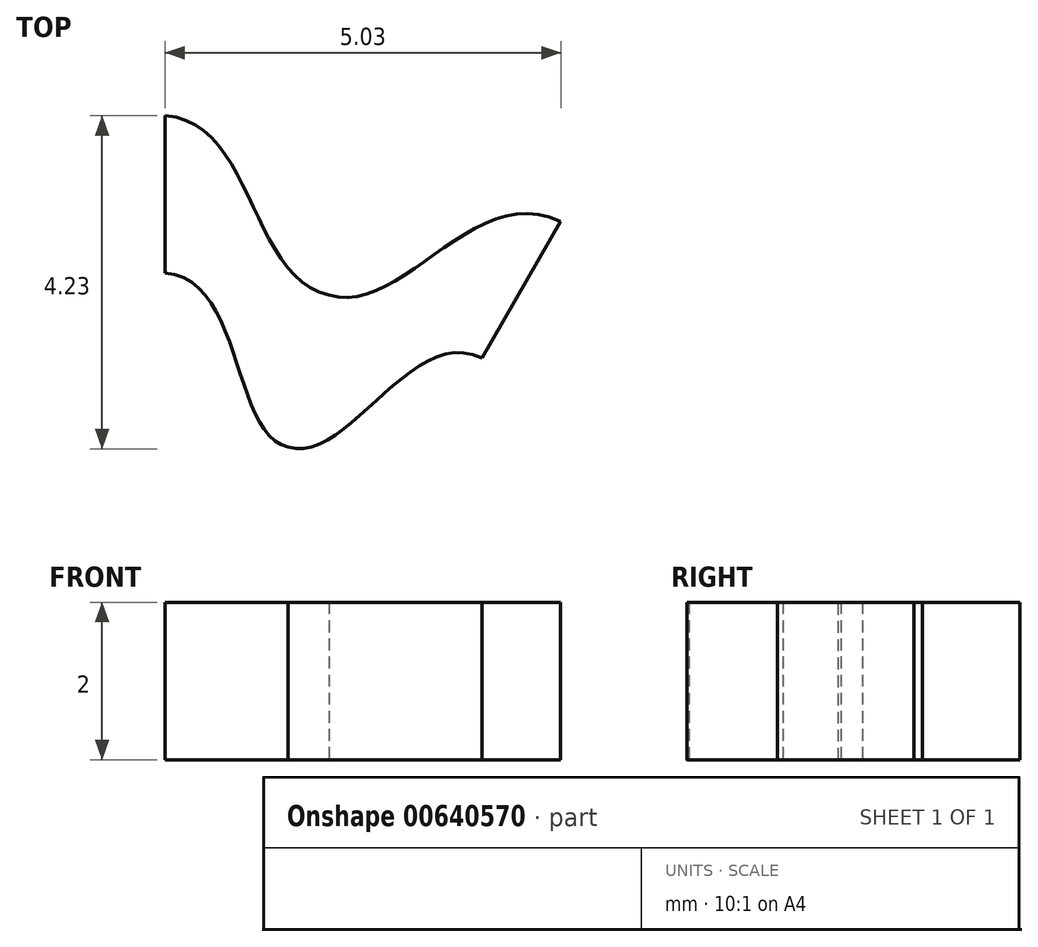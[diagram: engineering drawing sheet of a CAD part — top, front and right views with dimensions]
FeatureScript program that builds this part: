
annotation { "Feature Type Name" : "Feature", "Feature Type Description" : "" }
export const myFeature = defineFeature(function(context is Context, id is Id, definition is map)
    precondition{}
    {
        {
            var Q0;
            Q0=qCreatedBy(makeId("Top.planeOp"),FACE);
            var sketch = newSketch(context, id + "F0", { "sketchPlane" : qUnion([Q0])});
            skCircle(sketch, "E0", {"center": v(0, 0) * mm, "radius": 8.05 * mm, "construction": true});
            skLineSegment(sketch, "E1", {"start": v(0, 0) * mm, "end": v(3.4, 12.7) * mm, "construction": true});
            skLineSegment(sketch, "E2", {"start": v(0, 0) * mm, "end": v(6.53, 11.3) * mm, "construction": true});
            skLineSegment(sketch, "E3", {"start": v(0, 8.05) * mm, "end": v(0, 10.05) * mm});
            skLineSegment(sketch, "E4", {"start": v(2.08, 7.78) * mm, "end": v(1.57, 5.84) * mm});
            skLineSegment(sketch, "E5", {"start": v(4.02, 6.97) * mm, "end": v(5.02, 8.7) * mm});
            skFitSpline(sketch, "E6", {"points": [v(0, 10.05) * mm, v(2.08, 7.78) * mm], "startDerivative": vector(3.37, -0.19) * mm, "endDerivative": vector(3, -0.6) * mm});
            skFitSpline(sketch, "E7", {"points": [v(2.08, 7.78) * mm, v(5.03, 8.7) * mm], "startDerivative": vector(2.71, -0.9) * mm, "endDerivative": vector(3.3, -1.64) * mm});
            skFitSpline(sketch, "E8", {"points": [v(0, 8.05) * mm, v(1.57, 5.84) * mm], "startDerivative": vector(3, -0.19) * mm, "endDerivative": vector(2.16, -0.44) * mm});
            skFitSpline(sketch, "E9", {"points": [v(1.57, 5.84) * mm, v(4.02, 6.97) * mm], "startDerivative": vector(2.24, -0.76) * mm, "endDerivative": vector(2.7, -1.34) * mm});
            skCircle(sketch, "E10", {"center": v(0, 0) * mm, "radius": 10.05 * mm, "construction": true});
            skCircle(sketch, "E11", {"center": v(0, 0) * mm, "radius": 6.05 * mm, "construction": true});
            skSolve(sketch);
        }
        {
            var Q0;
            Q0 = qSketchRegion(id + "F0", true);
            extrude(context, id + "F1", {"entities" : qUnion([Q0]), "depth" : 2 * mm, "offsetDistance" : 25 * mm});
        }
        {
            var Q0;
            Q0=qCreatedBy(makeId("Right.planeOp"),FACE);
            var sketch = newSketch(context, id + "F2", { "sketchPlane" : qUnion([Q0])});
            skLineSegment(sketch, "E12", {"start": v(0, 0) * mm, "end": v(0, -47.48) * mm});
            skSolve(sketch);
        }
    });
